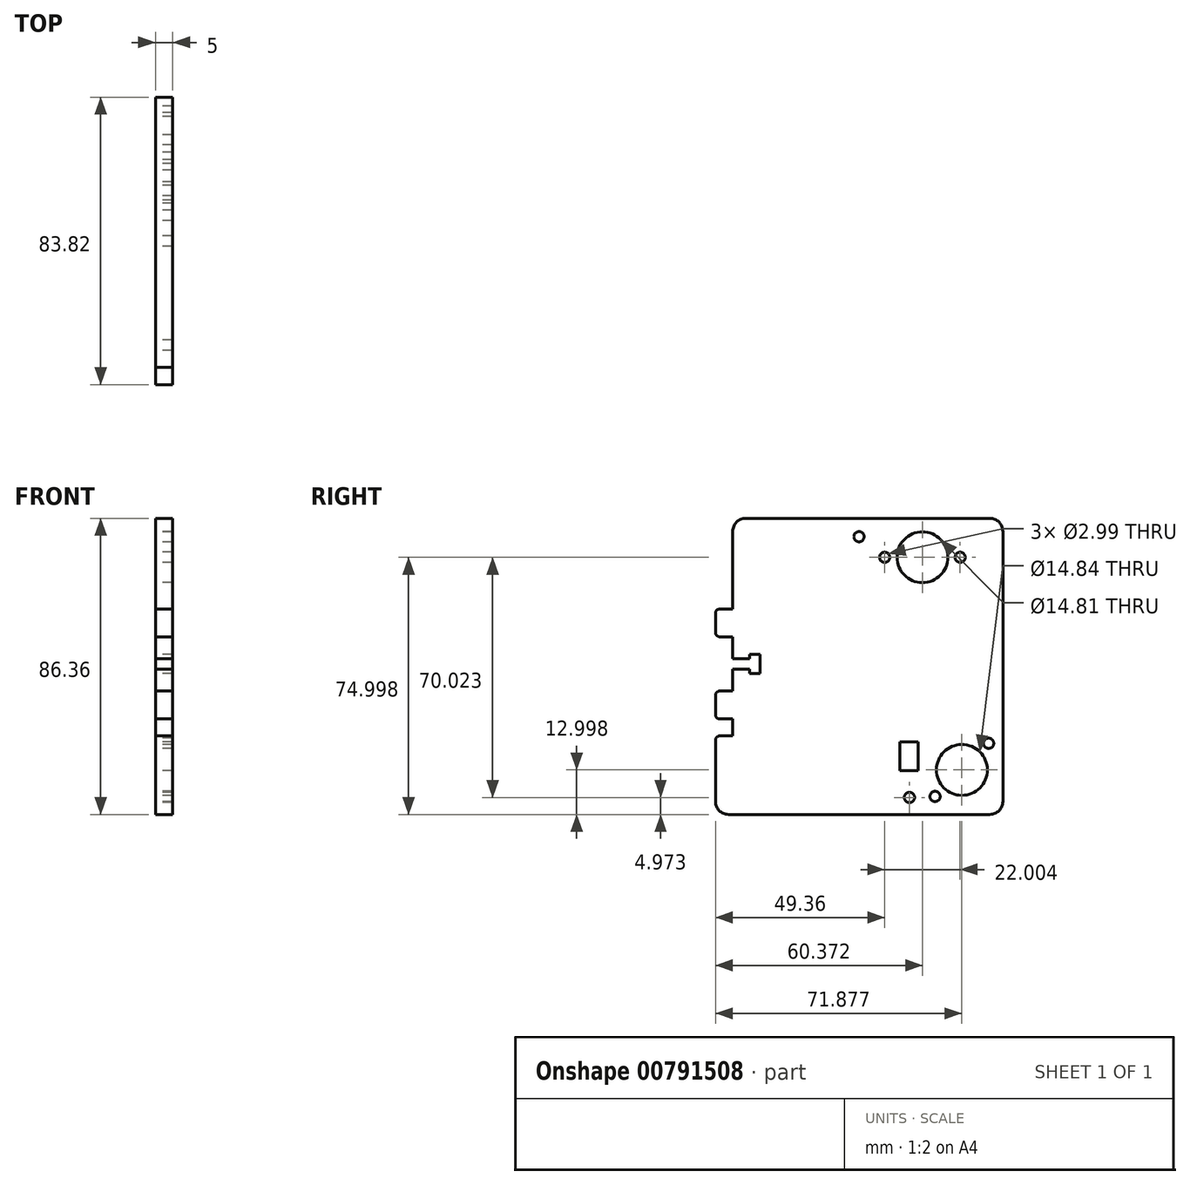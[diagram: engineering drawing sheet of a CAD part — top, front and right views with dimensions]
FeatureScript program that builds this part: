
annotation { "Feature Type Name" : "Feature", "Feature Type Description" : "" }
export const myFeature = defineFeature(function(context is Context, id is Id, definition is map)
    precondition{}
    {
        {
            var Q0;
            Q0=qCreatedBy(makeId("Right.planeOp"),FACE);
            var sketch = newSketch(context, id + "F0", { "sketchPlane" : qUnion([Q0])});
            skLineSegment(sketch, "E0.bottom", {"start": v(22.2, 43.4) * mm, "end": v(-48.97, 43.4) * mm});
            skLineSegment(sketch, "E0.top", {"start": v(22.2, -42.97) * mm, "end": v(-54, -42.97) * mm});
            skLineSegment(sketch, "E0.left", {"start": v(26, 39.58) * mm, "end": v(26, -39.16) * mm});
            skLineSegment(sketch, "E0.right", {"start": v(-57.82, 15.7) * mm, "end": v(-57.82, 10.11) * mm});
            skCircle(sketch, "E1", {"center": v(-15.94, 38.03) * mm, "radius": 1.5 * mm});
            skPoint(sketch, "E1.first.point", {"position": v(-17.25, 38.76) * mm});
            skPoint(sketch, "E1.second.point", {"position": v(-14.53, 38.54) * mm});
            skPoint(sketch, "E1.third.point", {"position": v(-16.05, 36.54) * mm});
            skCircle(sketch, "E2", {"center": v(-8.46, 32.03) * mm, "radius": 1.5 * mm});
            skPoint(sketch, "E2.first.point", {"position": v(-9.76, 32.76) * mm});
            skPoint(sketch, "E2.second.point", {"position": v(-7.05, 32.54) * mm});
            skPoint(sketch, "E2.third.point", {"position": v(-8.57, 30.53) * mm});
            skCircle(sketch, "E3", {"center": v(13.54, 32.03) * mm, "radius": 1.5 * mm});
            skPoint(sketch, "E3.first.point", {"position": v(12.24, 32.75) * mm});
            skPoint(sketch, "E3.second.point", {"position": v(14.95, 32.55) * mm});
            skPoint(sketch, "E3.third.point", {"position": v(13.44, 30.53) * mm});
            skCircle(sketch, "E4", {"center": v(2.55, 32.03) * mm, "radius": 7.4 * mm});
            skPoint(sketch, "E4.first.point", {"position": v(-3.94, 35.6) * mm});
            skPoint(sketch, "E4.second.point", {"position": v(9.27, 35.14) * mm});
            skPoint(sketch, "E4.third.point", {"position": v(2.35, 24.62) * mm});
            skCircle(sketch, "E5", {"center": v(21.87, -22.2) * mm, "radius": 1.5 * mm});
            skPoint(sketch, "E5.first.point", {"position": v(20.55, -21.48) * mm});
            skPoint(sketch, "E5.second.point", {"position": v(23.27, -21.69) * mm});
            skPoint(sketch, "E5.third.point", {"position": v(21.76, -23.7) * mm});
            skCircle(sketch, "E6", {"center": v(14.06, -29.97) * mm, "radius": 7.42 * mm});
            skPoint(sketch, "E6.first.point", {"position": v(7.53, -26.44) * mm});
            skPoint(sketch, "E6.second.point", {"position": v(20.82, -26.92) * mm});
            skPoint(sketch, "E6.third.point", {"position": v(14.1, -37.4) * mm});
            skCircle(sketch, "E7", {"center": v(6.24, -37.7) * mm, "radius": 1.5 * mm});
            skPoint(sketch, "E7.first.point", {"position": v(4.92, -36.98) * mm});
            skPoint(sketch, "E7.second.point", {"position": v(7.65, -37.2) * mm});
            skPoint(sketch, "E7.third.point", {"position": v(6.12, -39.2) * mm});
            skCircle(sketch, "E8", {"center": v(-1.24, -38) * mm, "radius": 1.5 * mm});
            skPoint(sketch, "E8.first.point", {"position": v(-2.54, -37.27) * mm});
            skPoint(sketch, "E8.second.point", {"position": v(-0.1, -37.03) * mm});
            skPoint(sketch, "E8.third.point", {"position": v(-1.33, -39.5) * mm});
            skLineSegment(sketch, "E9.bottom", {"start": v(-3.98, -21.76) * mm, "end": v(1.26, -21.76) * mm});
            skLineSegment(sketch, "E9.top", {"start": v(-3.98, -30.16) * mm, "end": v(1.26, -30.16) * mm});
            skLineSegment(sketch, "E9.left", {"start": v(-3.98, -21.76) * mm, "end": v(-3.98, -30.16) * mm});
            skLineSegment(sketch, "E9.right", {"start": v(1.26, -21.76) * mm, "end": v(1.26, -30.16) * mm});
            skPoint(sketch, "E10.visualSharp", {"position": v(26, -42.97) * mm});
            skArc(sketch, "E10.filletArc", {"start": v(22.2, -42.97) * mm, "mid": v(24.89, -41.85) * mm, "end": v(26, -39.16) * mm});
            skPoint(sketch, "E11.visualSharp", {"position": v(26, 43.4) * mm});
            skArc(sketch, "E11.filletArc", {"start": v(26, 39.58) * mm, "mid": v(24.89, 42.28) * mm, "end": v(22.2, 43.4) * mm});
            skPoint(sketch, "E12.visualSharp", {"position": v(-57.82, -42.97) * mm});
            skArc(sketch, "E12.filletArc", {"start": v(-57.82, -39.16) * mm, "mid": v(-56.7, -41.85) * mm, "end": v(-54, -42.97) * mm});
            skLineSegment(sketch, "E13.bottom", {"start": v(-52.78, 16.96) * mm, "end": v(-56.55, 16.96) * mm});
            skLineSegment(sketch, "E13.left", {"start": v(-52.78, 16.96) * mm, "end": v(-52.78, 39.58) * mm});
            skLineSegment(sketch, "E14.bottom", {"start": v(-52.78, -6.98) * mm, "end": v(-56.55, -6.98) * mm});
            skLineSegment(sketch, "E14.top", {"start": v(-52.78, 8.84) * mm, "end": v(-56.55, 8.84) * mm});
            skLineSegment(sketch, "E14.left", {"start": v(-52.78, -6.98) * mm, "end": v(-52.78, -0.58) * mm});
            skLineSegment(sketch, "E15.bottom", {"start": v(-47.8, -0.58) * mm, "end": v(-52.78, -0.58) * mm});
            skLineSegment(sketch, "E15.top", {"start": v(-47.8, 2.41) * mm, "end": v(-52.78, 2.41) * mm});
            skLineSegment(sketch, "E16.bottom", {"start": v(-44.8, -1.8) * mm, "end": v(-47.8, -1.8) * mm});
            skLineSegment(sketch, "E16.top", {"start": v(-44.8, 3.67) * mm, "end": v(-47.8, 3.67) * mm});
            skLineSegment(sketch, "E16.left", {"start": v(-44.8, -1.8) * mm, "end": v(-44.8, 3.67) * mm});
            skLineSegment(sketch, "E16.right", {"start": v(-47.8, -1.8) * mm, "end": v(-47.8, -0.58) * mm});
            skLineSegment(sketch, "E17.bottom", {"start": v(-52.82, -20.06) * mm, "end": v(-56.55, -20.06) * mm});
            skLineSegment(sketch, "E17.top", {"start": v(-52.82, -15.13) * mm, "end": v(-56.55, -15.13) * mm});
            skLineSegment(sketch, "E17.left", {"start": v(-52.82, -20.06) * mm, "end": v(-52.82, -15.13) * mm});
            skLineSegment(sketch, "E18.trimOffspring", {"start": v(-47.8, 2.41) * mm, "end": v(-47.8, 3.67) * mm});
            skLineSegment(sketch, "E19.trimOffspring", {"start": v(-52.78, 2.41) * mm, "end": v(-52.78, 8.84) * mm});
            skPoint(sketch, "E20.visualSharp", {"position": v(-52.78, 43.4) * mm});
            skArc(sketch, "E20.filletArc", {"start": v(-48.97, 43.4) * mm, "mid": v(-51.66, 42.28) * mm, "end": v(-52.78, 39.58) * mm});
            skLineSegment(sketch, "E21.trimOffspring", {"start": v(-57.82, -8.25) * mm, "end": v(-57.82, -13.86) * mm});
            skLineSegment(sketch, "E22.trimOffspring", {"start": v(-57.82, -21.33) * mm, "end": v(-57.82, -39.16) * mm});
            skPoint(sketch, "E23.visualSharp", {"position": v(-57.82, -20.06) * mm});
            skArc(sketch, "E23.filletArc", {"start": v(-56.55, -20.06) * mm, "mid": v(-57.45, -20.43) * mm, "end": v(-57.82, -21.33) * mm});
            skPoint(sketch, "E24.visualSharp", {"position": v(-57.82, -15.13) * mm});
            skArc(sketch, "E24.filletArc", {"start": v(-57.82, -13.86) * mm, "mid": v(-57.45, -14.76) * mm, "end": v(-56.55, -15.13) * mm});
            skPoint(sketch, "E25.orphan", {"position": v(-57.84, 16.96) * mm});
            skPoint(sketch, "E26.orphan", {"position": v(-57.84, 8.84) * mm});
            skPoint(sketch, "E27.visualSharp", {"position": v(-57.82, -6.98) * mm});
            skArc(sketch, "E27.filletArc", {"start": v(-56.55, -6.98) * mm, "mid": v(-57.45, -7.35) * mm, "end": v(-57.82, -8.25) * mm});
            skPoint(sketch, "E28.visualSharp", {"position": v(-57.82, 8.84) * mm});
            skArc(sketch, "E28.filletArc", {"start": v(-57.82, 10.11) * mm, "mid": v(-57.45, 9.21) * mm, "end": v(-56.55, 8.84) * mm});
            skPoint(sketch, "E29.visualSharp", {"position": v(-57.82, 16.96) * mm});
            skArc(sketch, "E29.filletArc", {"start": v(-56.55, 16.96) * mm, "mid": v(-57.45, 16.6) * mm, "end": v(-57.82, 15.7) * mm});
            skSolve(sketch);
        }
        {
            var Q0;
            Q0 = qSketchRegion(id + "F0", true);
            extrude(context, id + "F1", {"entities" : qUnion([Q0]), "depth" : 5 * mm, "offsetDistance" : 25.4 * mm});
        }
    });
